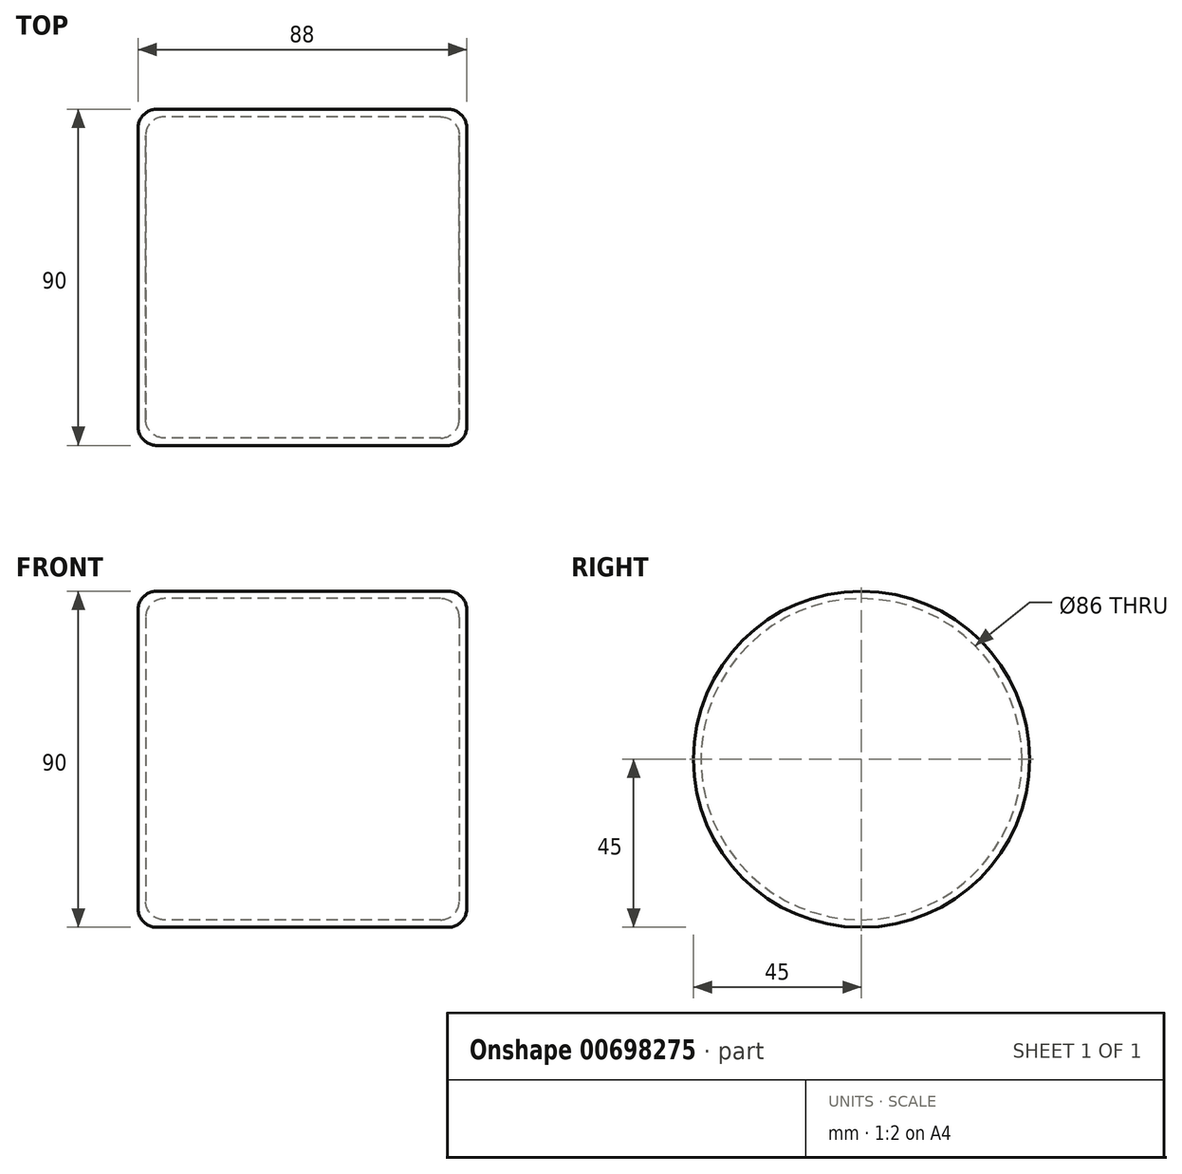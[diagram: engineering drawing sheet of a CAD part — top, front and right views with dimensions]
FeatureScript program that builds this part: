
annotation { "Feature Type Name" : "Feature", "Feature Type Description" : "" }
export const myFeature = defineFeature(function(context is Context, id is Id, definition is map)
    precondition{}
    {
        {
            var Q0;
            Q0=qCreatedBy(makeId("Front.planeOp"),FACE);
            var sketch = newSketch(context, id + "F0", { "sketchPlane" : qUnion([Q0])});
            skLineSegment(sketch, "E0", {"start": v(0, 0) * mm, "end": v(88, 0) * mm, "construction": true});
            skLineSegment(sketch, "E1", {"start": v(0, 0) * mm, "end": v(0, 40) * mm});
            skLineSegment(sketch, "E2", {"start": v(5, 45) * mm, "end": v(83, 45) * mm});
            skLineSegment(sketch, "E3", {"start": v(88, 40) * mm, "end": v(88, 0) * mm});
            skLineSegment(sketch, "E4", {"start": v(0, 0) * mm, "end": v(2, 0) * mm});
            skLineSegment(sketch, "E5.0", {"start": v(86, 38) * mm, "end": v(86, 0) * mm});
            skLineSegment(sketch, "E5.1", {"start": v(7, 43) * mm, "end": v(81, 43) * mm});
            skLineSegment(sketch, "E5.2", {"start": v(2, 0) * mm, "end": v(2, 38) * mm});
            skLineSegment(sketch, "E6", {"start": v(86, 0) * mm, "end": v(88, 0) * mm});
            skPoint(sketch, "E7.visualSharp", {"position": v(2, 43) * mm});
            skArc(sketch, "E7.filletArc", {"start": v(7, 43) * mm, "mid": v(3.46, 41.54) * mm, "end": v(2, 38) * mm});
            skPoint(sketch, "E8.visualSharp", {"position": v(0, 45) * mm});
            skArc(sketch, "E8.filletArc", {"start": v(5, 45) * mm, "mid": v(1.46, 43.54) * mm, "end": v(0, 40) * mm});
            skPoint(sketch, "E9.visualSharp", {"position": v(88, 45) * mm});
            skArc(sketch, "E9.filletArc", {"start": v(88, 40) * mm, "mid": v(86.54, 43.54) * mm, "end": v(83, 45) * mm});
            skPoint(sketch, "E10.visualSharp", {"position": v(86, 43) * mm});
            skArc(sketch, "E10.filletArc", {"start": v(86, 38) * mm, "mid": v(84.54, 41.54) * mm, "end": v(81, 43) * mm});
            skSolve(sketch);
        }
        {
            var Q0;
            Q0 = qSketchRegion(id + "F0", true);
            var Q1;
            Q1=sQuery(id+"F0.wireOp",EDGE,"E0");
            revolve(context, id + "F1", {"entities" : qUnion([Q0]), "axis" : qUnion([Q1]), "revolveType" : RevolveType.FULL});
        }
    });
